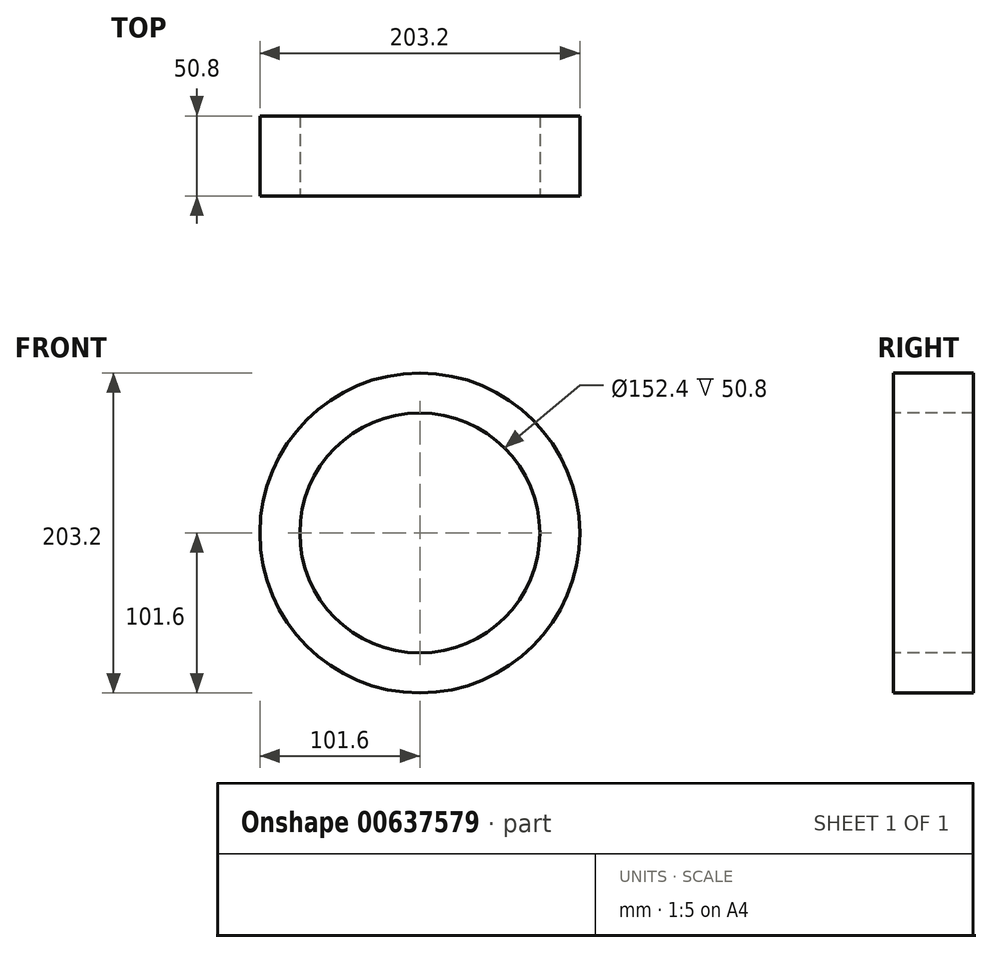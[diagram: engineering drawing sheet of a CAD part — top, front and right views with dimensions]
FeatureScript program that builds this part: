
annotation { "Feature Type Name" : "Feature", "Feature Type Description" : "" }
export const myFeature = defineFeature(function(context is Context, id is Id, definition is map)
    precondition{}
    {
        {
            var Q0;
            Q0=qCreatedBy(makeId("Top.planeOp"),FACE);
            var sketch = newSketch(context, id + "F0", { "sketchPlane" : qUnion([Q0])});
            skLineSegment(sketch, "E0.bottom", {"start": v(76.2, 0) * mm, "end": v(101.6, 0) * mm});
            skLineSegment(sketch, "E0.top", {"start": v(76.2, 50.8) * mm, "end": v(101.6, 50.8) * mm});
            skLineSegment(sketch, "E0.left", {"start": v(76.2, 0) * mm, "end": v(76.2, 50.8) * mm});
            skLineSegment(sketch, "E0.right", {"start": v(101.6, 0) * mm, "end": v(101.6, 50.8) * mm});
            skLineSegment(sketch, "E1", {"start": v(0, 0) * mm, "end": v(0, 142.33) * mm, "construction": true});
            skSolve(sketch);
        }
        {
            var Q0;
            Q0=makeQuery(id+"F0.imprint","IMPRINT",FACE,{"disambiguationData":[TD([[makeQuery(id+"F0.imprint","IMPRINT",EDGE,{"derivedFrom":sQuery(id+"F0.wireOp",EDGE,"E0.bottom")}),1.0]])]});
            var Q1;
            Q1=sQuery(id+"F0.wireOp",EDGE,"E1");
            revolve(context, id + "F1", {"entities" : qUnion([Q0]), "axis" : qUnion([Q1]), "revolveType" : RevolveType.FULL});
        }
    });
